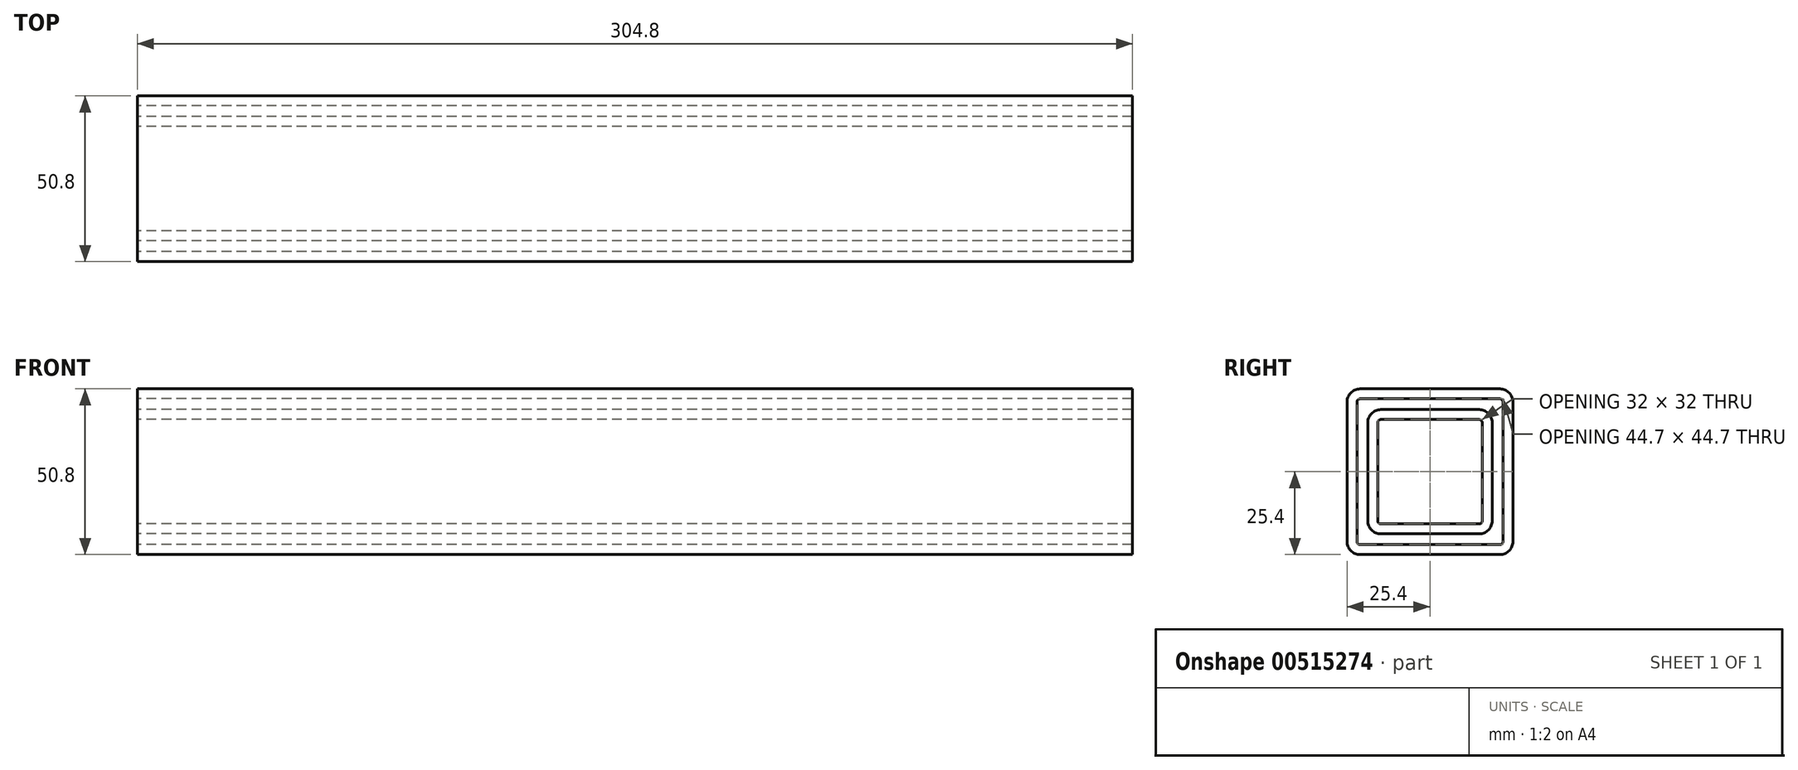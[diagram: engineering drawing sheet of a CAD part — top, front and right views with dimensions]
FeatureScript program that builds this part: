
annotation { "Feature Type Name" : "Feature", "Feature Type Description" : "" }
export const myFeature = defineFeature(function(context is Context, id is Id, definition is map)
    precondition{}
    {
        {
            var Q0;
            Q0=qCreatedBy(makeId("Right.planeOp"),FACE);
            var sketch = newSketch(context, id + "F0", { "sketchPlane" : qUnion([Q0])});
            skLineSegment(sketch, "E0.bottom", {"start": v(-21.43, 25.4) * mm, "end": v(21.43, 25.4) * mm});
            skLineSegment(sketch, "E0.top", {"start": v(-21.43, -25.4) * mm, "end": v(21.43, -25.4) * mm});
            skLineSegment(sketch, "E0.left", {"start": v(-25.4, 21.43) * mm, "end": v(-25.4, -21.43) * mm});
            skLineSegment(sketch, "E0.right", {"start": v(25.4, 21.43) * mm, "end": v(25.4, -21.43) * mm});
            skPoint(sketch, "E1.visualSharp", {"position": v(25.4, 25.4) * mm});
            skArc(sketch, "E1.filletArc", {"start": v(25.4, 21.43) * mm, "mid": v(24.24, 24.24) * mm, "end": v(21.43, 25.4) * mm});
            skPoint(sketch, "E2.visualSharp", {"position": v(-25.4, 25.4) * mm});
            skArc(sketch, "E2.filletArc", {"start": v(-21.43, 25.4) * mm, "mid": v(-24.24, 24.24) * mm, "end": v(-25.4, 21.43) * mm});
            skPoint(sketch, "E3.visualSharp", {"position": v(-25.4, -25.4) * mm});
            skArc(sketch, "E3.filletArc", {"start": v(-25.4, -21.43) * mm, "mid": v(-24.24, -24.24) * mm, "end": v(-21.43, -25.4) * mm});
            skPoint(sketch, "E4.visualSharp", {"position": v(25.4, -25.4) * mm});
            skArc(sketch, "E4.filletArc", {"start": v(21.43, -25.4) * mm, "mid": v(24.24, -24.24) * mm, "end": v(25.4, -21.43) * mm});
            skLineSegment(sketch, "E5.bottom", {"start": v(-21.43, -22.35) * mm, "end": v(21.43, -22.35) * mm});
            skLineSegment(sketch, "E5.top", {"start": v(-21.43, 22.35) * mm, "end": v(21.43, 22.35) * mm});
            skLineSegment(sketch, "E5.left", {"start": v(-22.35, -21.43) * mm, "end": v(-22.35, 21.43) * mm});
            skLineSegment(sketch, "E5.right", {"start": v(22.35, -21.43) * mm, "end": v(22.35, 21.43) * mm});
            skPoint(sketch, "E5.middle", {"position": v(0, 0) * mm});
            skPoint(sketch, "E6.visualSharp", {"position": v(22.35, 22.35) * mm});
            skArc(sketch, "E6.filletArc", {"start": v(22.35, 21.43) * mm, "mid": v(22.08, 22.08) * mm, "end": v(21.43, 22.35) * mm});
            skPoint(sketch, "E7.visualSharp", {"position": v(-22.35, 22.35) * mm});
            skArc(sketch, "E7.filletArc", {"start": v(-21.43, 22.35) * mm, "mid": v(-22.08, 22.08) * mm, "end": v(-22.35, 21.43) * mm});
            skPoint(sketch, "E8.visualSharp", {"position": v(-22.35, -22.35) * mm});
            skArc(sketch, "E8.filletArc", {"start": v(-22.35, -21.43) * mm, "mid": v(-22.08, -22.08) * mm, "end": v(-21.43, -22.35) * mm});
            skPoint(sketch, "E9.visualSharp", {"position": v(22.35, -22.35) * mm});
            skArc(sketch, "E9.filletArc", {"start": v(21.43, -22.35) * mm, "mid": v(22.08, -22.08) * mm, "end": v(22.35, -21.43) * mm});
            skLineSegment(sketch, "E10", {"start": v(0, 25.4) * mm, "end": v(0, -25.4) * mm, "construction": true});
            skLineSegment(sketch, "E11", {"start": v(-25.4, 0) * mm, "end": v(25.4, 0) * mm, "construction": true});
            skSolve(sketch);
        }
        {
            var Q0;
            Q0=qSketchRegion(id+"F0",true);
            extrude(context, id + "F1", {"entities" : qUnion([Q0]), "depth" : 304.8 * mm, "offsetDistance" : 25.4 * mm});
        }
        {
            var Q0;
            Q0=qCreatedBy(makeId("Right.planeOp"),FACE);
            var sketch = newSketch(context, id + "F2", { "sketchPlane" : qUnion([Q0])});
            skLineSegment(sketch, "E12.bottom", {"start": v(15.08, 19.05) * mm, "end": v(-15.08, 19.05) * mm});
            skLineSegment(sketch, "E12.top", {"start": v(15.08, -19.05) * mm, "end": v(-15.08, -19.05) * mm});
            skLineSegment(sketch, "E12.left", {"start": v(19.05, 15.08) * mm, "end": v(19.05, -15.08) * mm});
            skLineSegment(sketch, "E12.right", {"start": v(-19.05, 15.08) * mm, "end": v(-19.05, -15.08) * mm});
            skLineSegment(sketch, "E13", {"start": v(0, 19.05) * mm, "end": v(0, -19.05) * mm, "construction": true});
            skLineSegment(sketch, "E14", {"start": v(19.05, 0) * mm, "end": v(-19.05, 0) * mm, "construction": true});
            skPoint(sketch, "E15.visualSharp", {"position": v(19.05, 19.05) * mm});
            skArc(sketch, "E15.filletArc", {"start": v(19.05, 15.08) * mm, "mid": v(17.89, 17.89) * mm, "end": v(15.08, 19.05) * mm});
            skPoint(sketch, "E16.visualSharp", {"position": v(-19.05, 19.05) * mm});
            skArc(sketch, "E16.filletArc", {"start": v(-15.08, 19.05) * mm, "mid": v(-17.89, 17.89) * mm, "end": v(-19.05, 15.08) * mm});
            skPoint(sketch, "E17.visualSharp", {"position": v(19.05, -19.05) * mm});
            skArc(sketch, "E17.filletArc", {"start": v(15.08, -19.05) * mm, "mid": v(17.89, -17.89) * mm, "end": v(19.05, -15.08) * mm});
            skPoint(sketch, "E18.visualSharp", {"position": v(-19.05, -19.05) * mm});
            skArc(sketch, "E18.filletArc", {"start": v(-19.05, -15.08) * mm, "mid": v(-17.89, -17.89) * mm, "end": v(-15.08, -19.05) * mm});
            skLineSegment(sketch, "E19.0", {"start": v(15.08, 16) * mm, "end": v(-15.08, 16) * mm});
            skLineSegment(sketch, "E19.1", {"start": v(16, 15.08) * mm, "end": v(16, -15.08) * mm});
            skLineSegment(sketch, "E19.2", {"start": v(15.08, -16) * mm, "end": v(-15.08, -16) * mm});
            skLineSegment(sketch, "E19.3", {"start": v(-16, 15.08) * mm, "end": v(-16, -15.08) * mm});
            skPoint(sketch, "E20.visualSharp", {"position": v(16, 16) * mm});
            skArc(sketch, "E20.filletArc", {"start": v(16, 15.08) * mm, "mid": v(15.73, 15.73) * mm, "end": v(15.08, 16) * mm});
            skPoint(sketch, "E21.visualSharp", {"position": v(-16, 16) * mm});
            skArc(sketch, "E21.filletArc", {"start": v(-15.08, 16) * mm, "mid": v(-15.73, 15.73) * mm, "end": v(-16, 15.08) * mm});
            skPoint(sketch, "E22.visualSharp", {"position": v(-16, -16) * mm});
            skArc(sketch, "E22.filletArc", {"start": v(-16, -15.08) * mm, "mid": v(-15.73, -15.73) * mm, "end": v(-15.08, -16) * mm});
            skPoint(sketch, "E23.visualSharp", {"position": v(16, -16) * mm});
            skArc(sketch, "E23.filletArc", {"start": v(15.08, -16) * mm, "mid": v(15.73, -15.73) * mm, "end": v(16, -15.08) * mm});
            skSolve(sketch);
        }
        {
            var Q0;
            Q0 = qSketchRegion(id + "F2", true);
            extrude(context, id + "F3", {"entities" : qUnion([Q0]), "depth" : 304.8 * mm, "offsetDistance" : 25.4 * mm});
        }
    });
